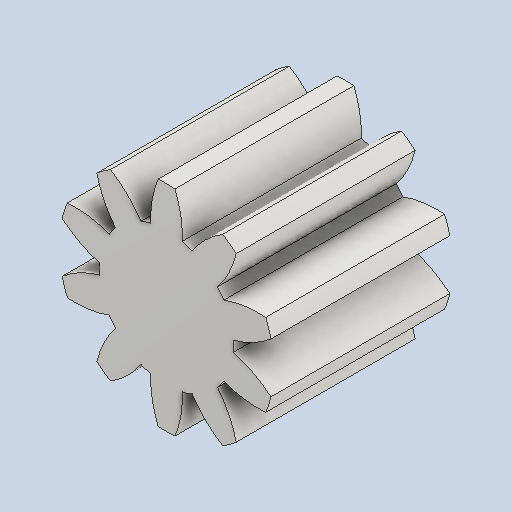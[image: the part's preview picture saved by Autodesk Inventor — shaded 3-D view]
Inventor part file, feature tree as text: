
AUTODESK INVENTOR PART (.ipt)
format: ipt  version: 2024 (Build 280153000, 153)  size: 216,576 bytes
history: native  units: mm (DEFAULTED — no unit token found)
features: plane x3, other x3, extrude x1, sketch x1
ambient origin geometry x8: Origin, YZ Plane, XZ Plane, XY Plane, X Axis, Y Axis, Z Axis, Center Point
bodies: Solid1 (feature_tree)
feature tree (8):
  extrude  "Extrusion1"  Depth=20.0mm TaperAngle=0.0deg
  plane  "Work Plane2"
  plane  "Work Plane8"
  plane  "Work Plane9"
  other  "Spur Gear"
  sketch  "Sketch1"  dims[d0=24.0mm d1=20.0mm d2=0.0mm d3=20.0mm d4=10.0mm d5=0.0mm d16=35.0mm d17=0.0mm d34=3.141593mm d39=0.0mm d41=0.0mm d43=35.0mm d46=35.0mm d47=0.0mm d48=0.0mm]
  other  "Srf1"
  other  "Pitch Diameter"
